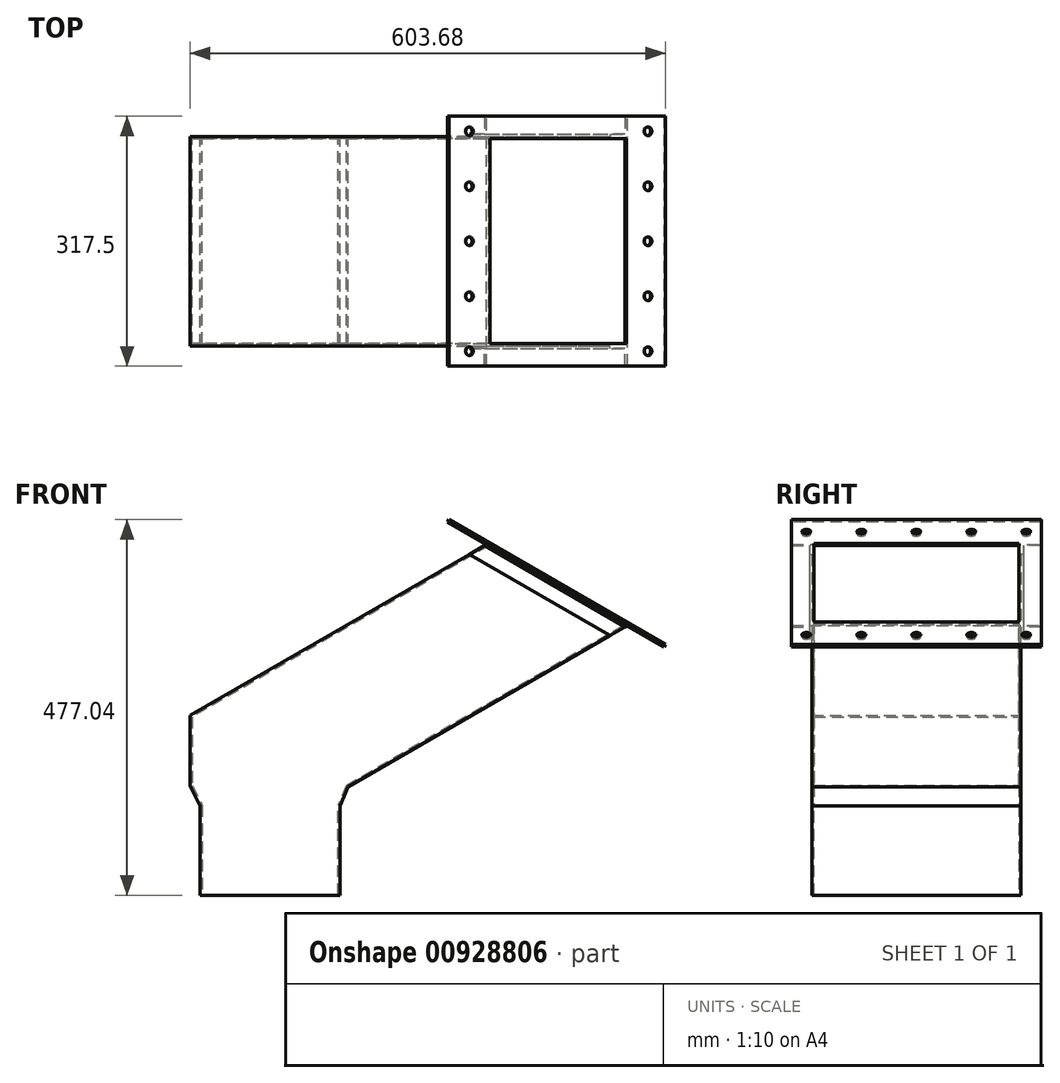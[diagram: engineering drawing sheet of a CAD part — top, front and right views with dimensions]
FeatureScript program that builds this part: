
annotation { "Feature Type Name" : "Feature", "Feature Type Description" : "" }
export const myFeature = defineFeature(function(context is Context, id is Id, definition is map)
    precondition{}
    {
        {
            var Q0;
            Q0=qCreatedBy(makeId("Front.planeOp"),FACE);
            var sketch = newSketch(context, id + "F0", { "sketchPlane" : qUnion([Q0])});
            skLineSegment(sketch, "E0", {"start": v(-317.85, 2733.04) * mm, "end": v(355.25, 2344.43) * mm});
            skLineSegment(sketch, "E1", {"start": v(355.25, 2344.43) * mm, "end": v(1028.35, 2733.04) * mm});
            skLineSegment(sketch, "E2", {"start": v(-317.85, 2733.04) * mm, "end": v(-317.85, 4597.4) * mm});
            skLineSegment(sketch, "E3", {"start": v(-317.85, 4597.4) * mm, "end": v(1028.35, 4597.4) * mm});
            skLineSegment(sketch, "E4", {"start": v(1028.35, 2733.04) * mm, "end": v(1028.35, 4597.4) * mm});
            skLineSegment(sketch, "E5", {"start": v(-317.85, 2733.04) * mm, "end": v(1028.35, 2733.04) * mm, "construction": true});
            skLineSegment(sketch, "E6", {"start": v(-317.85, 2739.4) * mm, "end": v(-368.65, 2739.4) * mm});
            skLineSegment(sketch, "E7", {"start": v(-368.65, 2733.04) * mm, "end": v(-368.65, 2739.4) * mm});
            skLineSegment(sketch, "E8", {"start": v(-368.65, 2733.04) * mm, "end": v(1079.15, 2733.04) * mm});
            skLineSegment(sketch, "E9", {"start": v(1079.15, 2739.4) * mm, "end": v(1079.15, 2733.04) * mm});
            skLineSegment(sketch, "E10", {"start": v(1079.15, 2739.4) * mm, "end": v(1028.35, 2739.4) * mm});
            skLineSegment(sketch, "E11", {"start": v(355.25, 4597.4) * mm, "end": v(355.25, 2344.43) * mm, "construction": true});
            skLineSegment(sketch, "E12", {"start": v(355.25, 2344.43) * mm, "end": v(0, 2139.33) * mm, "construction": true});
            skLineSegment(sketch, "E13", {"start": v(0, 2088) * mm, "end": v(0, 0) * mm, "construction": true});
            skLineSegment(sketch, "E14", {"start": v(-1118.25, 0) * mm, "end": v(0, 0) * mm, "construction": true});
            skLineSegment(sketch, "E15", {"start": v(-317.85, 2739.4) * mm, "end": v(-317.85, 2088) * mm, "construction": true});
            skLineSegment(sketch, "E16", {"start": v(-317.85, 2088) * mm, "end": v(-88.9, 2088) * mm, "construction": true});
            skLineSegment(sketch, "E17", {"start": v(-88.9, 2088) * mm, "end": v(0, 2088) * mm, "construction": true});
            skLineSegment(sketch, "E18", {"start": v(0, 2088) * mm, "end": v(0, 2139.33) * mm, "construction": true});
            skLineSegment(sketch, "E19", {"start": v(0, 2088) * mm, "end": v(0, 2088) * mm});
            skPoint(sketch, "E20", {"position": v(-203.38, 2088) * mm});
            skSolve(sketch);
        }
        {
            var Q0;
            Q0=qCreatedBy(makeId("Right.planeOp"),FACE);
            var sketch = newSketch(context, id + "F1", { "sketchPlane" : qUnion([Q0])});
            skLineSegment(sketch, "E21", {"start": v(0, 2549.53) * mm, "end": v(-535.95, 2549.53) * mm});
            skSolve(sketch);
        }
        {
            var Q0;
            Q0=sQuery(id+"F1.wireOp",VERTEX,"E21.end");
            var Q1;
            Q1=sQuery(id+"F0.wireOp",VERTEX,"E0.start");
            var Q2;
            Q2=sQuery(id+"F0.wireOp",VERTEX,"E0.end");
            cPlane(context, id + "F2", {"entities" : qUnion([Q0, Q1, Q2]), "cplaneType" : CPlaneType.THREE_POINT, "offset" : 3.17 * mm, "oppositeDirection" : true, "width" : 152.4 * mm, "height" : 152.4 * mm});
        }
        {
            var Q0;
            Q0=qCreatedBy(id+"F2.planeOp",FACE);
            var sketch = newSketch(context, id + "F3", { "sketchPlane" : qUnion([Q0])});
            skLineSegment(sketch, "E22.bottom", {"start": v(-1067.66, -130.18) * mm, "end": v(-1067.66, 130.17) * mm});
            skLineSegment(sketch, "E22.top", {"start": v(-867.64, -130.18) * mm, "end": v(-867.64, 130.17) * mm});
            skLineSegment(sketch, "E22.left", {"start": v(-1067.66, 130.17) * mm, "end": v(-867.64, 130.17) * mm});
            skLineSegment(sketch, "E22.right", {"start": v(-1067.66, -130.18) * mm, "end": v(-867.64, -130.18) * mm});
            skLineSegment(sketch, "E23.bottom", {"start": v(-1127.99, 158.75) * mm, "end": v(-810.49, 158.75) * mm});
            skLineSegment(sketch, "E23.top", {"start": v(-1127.99, -158.75) * mm, "end": v(-810.49, -158.75) * mm});
            skLineSegment(sketch, "E23.left", {"start": v(-1127.99, 158.75) * mm, "end": v(-1127.99, -158.75) * mm});
            skLineSegment(sketch, "E23.right", {"start": v(-810.49, 158.75) * mm, "end": v(-810.49, -158.75) * mm});
            skLineSegment(sketch, "E24", {"start": v(-967.65, 130.17) * mm, "end": v(-967.65, 158.75) * mm, "construction": true});
            skLineSegment(sketch, "E25", {"start": v(-810.49, 0) * mm, "end": v(-867.64, 0) * mm, "construction": true});
            skSolve(sketch);
        }
        {
            var Q0;
            Q0=qSketchRegion(id+"F3",true);
            extrude(context, id + "F4", {"entities" : qUnion([Q0]), "oppositeDirection" : true, "depth" : 3.17 * mm, "offsetDistance" : 25.4 * mm});
        }
        {
            var Q0;
            Q0=qCreatedBy(makeId("Front.planeOp"),FACE);
            var sketch = newSketch(context, id + "F5", { "sketchPlane" : qUnion([Q0])});
            skLineSegment(sketch, "E26", {"start": v(-186.23, 2062.6) * mm, "end": v(-13.77, 2062.6) * mm, "construction": true});
            skLineSegment(sketch, "E27", {"start": v(-13.77, 2062.6) * mm, "end": v(-13.77, 2113.4) * mm});
            skLineSegment(sketch, "E28", {"start": v(-3.07, 2138.8) * mm, "end": v(-13.77, 2113.4) * mm});
            skLineSegment(sketch, "E29", {"start": v(-3.07, 2138.8) * mm, "end": v(351, 2343.22) * mm});
            skLineSegment(sketch, "E30", {"start": v(351, 2343.22) * mm, "end": v(177.77, 2443.23) * mm});
            skLineSegment(sketch, "E31", {"start": v(177.77, 2443.23) * mm, "end": v(-198.93, 2225.74) * mm});
            skLineSegment(sketch, "E32", {"start": v(-198.93, 2225.74) * mm, "end": v(-198.93, 2138.8) * mm});
            skLineSegment(sketch, "E33", {"start": v(-198.93, 2138.8) * mm, "end": v(-186.23, 2113.4) * mm});
            skLineSegment(sketch, "E34", {"start": v(-186.23, 2113.4) * mm, "end": v(-186.23, 2062.6) * mm});
            skLineSegment(sketch, "E35", {"start": v(-100, 2062.6) * mm, "end": v(-100, 2182.85) * mm, "construction": true});
            skPoint(sketch, "E35.endSnap0", {"position": v(351, 2343.22) * mm});
            skLineSegment(sketch, "E36", {"start": v(-100, 2182.85) * mm, "end": v(264.38, 2393.23) * mm, "construction": true});
            skLineSegment(sketch, "E37", {"start": v(-100, 2088) * mm, "end": v(-100, 2062.6) * mm, "construction": true});
            skLineSegment(sketch, "E38.bottom", {"start": v(-186.23, 2062.6) * mm, "end": v(-13.77, 2062.6) * mm});
            skLineSegment(sketch, "E38.top", {"start": v(-186.23, 1999.1) * mm, "end": v(-13.77, 1999.1) * mm});
            skLineSegment(sketch, "E38.left", {"start": v(-186.23, 2062.6) * mm, "end": v(-186.23, 1999.1) * mm});
            skLineSegment(sketch, "E38.right", {"start": v(-13.77, 2062.6) * mm, "end": v(-13.77, 1999.1) * mm});
            skSolve(sketch);
        }
        {
            var Q0;
            Q0=qSketchRegion(id+"F5",true);
            extrude(context, id + "F6", {"entities" : qUnion([Q0]), "endBound" : BoundingType.SYMMETRIC, "depth" : 260.35 * mm, "offsetDistance" : 25.4 * mm});
        }
        {
            var Q0;
            Q0=makeQuery(id+"F6.opExtrude","SWEPT_FACE",FACE,{"disambiguationData":[OSD([sQuery(id+"F5.wireOp",EDGE,"E30")])]});
            var Q1;
            Q1=makeQuery(id+"F6.opExtrude","SWEPT_FACE",FACE,{"disambiguationData":[OSD([sQuery(id+"F5.wireOp",EDGE,"E26")])]});
            var Q2;
            Q2=makeQuery(id+"F6.opExtrude","SWEPT_FACE",FACE,{"disambiguationData":[OSD([sQuery(id+"F5.wireOp",EDGE,"E38.top")])]});
            shell(context, id + "F7", {"entities" : qUnion([Q0, Q1, Q2]), "thickness" : 2.67 * mm, "oppositeDirection" : true});
        }
        {
            var Q0;
            Q0=makeQuery(id+"F6.opExtrude","SWEPT_FACE",FACE,{"disambiguationData":[OSD([sQuery(id+"F5.wireOp",EDGE,"E31")])]});
            var sketch = newSketch(context, id + "F8", { "sketchPlane" : qUnion([Q0])});
            skLineSegment(sketch, "E39", {"start": v(1374.03, -132.84) * mm, "end": v(1374.03, -158.24) * mm});
            skLineSegment(sketch, "E40", {"start": v(1374.03, -158.24) * mm, "end": v(1370.85, -158.24) * mm});
            skLineSegment(sketch, "E41", {"start": v(1370.85, -158.24) * mm, "end": v(1370.85, -136.02) * mm});
            skLineSegment(sketch, "E42", {"start": v(1370.85, -136.02) * mm, "end": v(1348.63, -136.02) * mm});
            skLineSegment(sketch, "E43", {"start": v(1348.63, -136.02) * mm, "end": v(1348.63, -132.84) * mm});
            skLineSegment(sketch, "E44", {"start": v(1348.63, -132.84) * mm, "end": v(1374.03, -132.84) * mm});
            skLineSegment(sketch, "E45", {"start": v(1374.03, 0) * mm, "end": v(1297.03, 0) * mm, "construction": true});
            skLineSegment(sketch, "E46.MirrorCS", {"start": v(1348.63, 136.02) * mm, "end": v(1348.63, 132.84) * mm});
            skLineSegment(sketch, "E47.MirrorCS", {"start": v(1374.03, 158.24) * mm, "end": v(1370.85, 158.24) * mm});
            skLineSegment(sketch, "E48.MirrorCS", {"start": v(1348.63, 132.84) * mm, "end": v(1374.03, 132.84) * mm});
            skLineSegment(sketch, "E49.MirrorCS", {"start": v(1370.85, 158.24) * mm, "end": v(1370.85, 136.02) * mm});
            skLineSegment(sketch, "E50.MirrorCS", {"start": v(1374.03, 132.84) * mm, "end": v(1374.03, 158.24) * mm});
            skLineSegment(sketch, "E51.MirrorCS", {"start": v(1370.85, 136.02) * mm, "end": v(1348.63, 136.02) * mm});
            skSolve(sketch);
        }
        {
            var Q0;
            Q0=qSketchRegion(id+"F8",true);
            var Q1;
            Q1=makeQuery(id+"F6.opExtrude","CAP_EDGE",EDGE,{"disambiguationData":[OSD([sQuery(id+"F5.wireOp",EDGE,"E30")])],"isStart":false});
            sweep(context, id + "F9", {"operationType" : NewBodyOperationType.ADD, "profiles" : qUnion([Q0]), "path" : qUnion([Q1])});
        }
        {
            var Q0;
            Q0=makeQuery(id+"F4.opExtrude","CAP_FACE",FACE,{"disambiguationData":[OSD([sQuery(id+"F3.wireOp",EDGE,"E22.bottom"),sQuery(id+"F3.wireOp",EDGE,"E22.top"),sQuery(id+"F3.wireOp",EDGE,"E22.left"),sQuery(id+"F3.wireOp",EDGE,"E22.right"),sQuery(id+"F3.wireOp",EDGE,"E23.bottom"),sQuery(id+"F3.wireOp",EDGE,"E23.top"),sQuery(id+"F3.wireOp",EDGE,"E23.left"),sQuery(id+"F3.wireOp",EDGE,"E23.right")])],"isStart":true});
            var sketch = newSketch(context, id + "F10", { "sketchPlane" : qUnion([Q0])});
            skCircle(sketch, "E52", {"center": v(-835.89, -139.7) * mm, "radius": 5.56 * mm});
            skCircle(sketch, "E53", {"center": v(-1097.83, -139.7) * mm, "radius": 5.56 * mm});
            skLineSegment(sketch, "E54", {"start": v(-867.64, -139.7) * mm, "end": v(-835.89, -139.7) * mm, "construction": true});
            skLineSegment(sketch, "E55", {"start": v(-810.49, -139.7) * mm, "end": v(-835.89, -139.7) * mm, "construction": true});
            skCircle(sketch, "E56.0.1.0", {"center": v(-1097.83, -69.85) * mm, "radius": 5.56 * mm});
            skCircle(sketch, "E56.0.1.1", {"center": v(-835.89, -69.85) * mm, "radius": 5.56 * mm});
            skCircle(sketch, "E56.0.2.0", {"center": v(-1097.83, 0) * mm, "radius": 5.56 * mm});
            skCircle(sketch, "E56.0.2.1", {"center": v(-835.89, 0) * mm, "radius": 5.56 * mm});
            skCircle(sketch, "E56.0.3.0", {"center": v(-1097.83, 69.85) * mm, "radius": 5.56 * mm});
            skCircle(sketch, "E56.0.3.1", {"center": v(-835.89, 69.85) * mm, "radius": 5.56 * mm});
            skCircle(sketch, "E56.0.4.0", {"center": v(-1097.83, 139.7) * mm, "radius": 5.56 * mm});
            skCircle(sketch, "E56.0.4.1", {"center": v(-835.89, 139.7) * mm, "radius": 5.56 * mm});
            skLineSegment(sketch, "E56.direction1", {"start": v(-1097.83, -139.7) * mm, "end": v(-1067.66, -139.7) * mm, "construction": true});
            skLineSegment(sketch, "E56.direction2", {"start": v(-1097.83, -139.7) * mm, "end": v(-1097.83, -69.85) * mm, "construction": true});
            skLineSegment(sketch, "E57", {"start": v(-835.89, 158.75) * mm, "end": v(-835.89, -139.7) * mm, "construction": true});
            skLineSegment(sketch, "E58", {"start": v(-835.89, -158.75) * mm, "end": v(-835.89, 139.7) * mm, "construction": true});
            skLineSegment(sketch, "E59", {"start": v(-1097.83, -139.7) * mm, "end": v(-1127.99, -139.7) * mm, "construction": true});
            skSolve(sketch);
        }
        {
            var Q0;
            Q0=qSketchRegion(id+"F10",true);
            extrude(context, id + "F11", {"entities" : qUnion([Q0]), "operationType" : NewBodyOperationType.REMOVE, "endBound" : BoundingType.UP_TO_NEXT, "oppositeDirection" : true, "depth" : 25.4 * mm, "offsetDistance" : 25.4 * mm});
        }
    });
